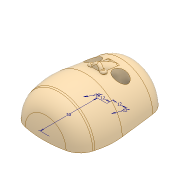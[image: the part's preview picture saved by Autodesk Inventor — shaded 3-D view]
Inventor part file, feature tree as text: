
AUTODESK INVENTOR PART (.ipt)
format: ipt  version: 2017 (Build 210142000, 142)  size: 386,560 bytes
history: native  units: mm
features: fillet x7, sketch x5, extrude x4, revolve x1, chamfer x1, thicken_offset x1
ambient origin geometry x8: Origin, YZ Plane, XZ Plane, XY Plane, X Axis, Y Axis, Z Axis, Center Point
bodies: Solid1 (feature_tree)
feature tree (19):
  revolve  "Revolution1"  [1 undecoded]
  fillet  "Fillet1"  Radius=30.0mm
  chamfer  "Chamfer1"  Distance=10.0mm Angle=45.0deg
  fillet  "Fillet2"  Radius=20.0mm
  fillet  "Fillet3"  Radius=60.0mm
  thicken_offset  "Thicken1"
  extrude  "Extrusion1"  Depth=4.0mm
  sketch  "Sketch3"  dims[d4=20.0mm d5=10.0mm d6=20.0mm d7=45.0deg d8=20.0mm d9=60.0mm]
  extrude  "Extrusion2"  Depth=1.5mm
  extrude  "Extrusion3"  Depth=1.5mm
  fillet  "Fillet4"  Radius=12.0mm
  fillet  "Fillet5"  Radius=12.0mm
  extrude  "Extrusion4"  Depth=1.5mm
  fillet  "Fillet6"  Radius=10.0mm
  fillet  "Fillet7"  Radius=10.0mm
  sketch  "Sketch1"  dims[d0=40.0mm d1=80.0mm d2=30.0mm]
  sketch  "Sketch2"  dims[d3=90.0deg]
  sketch  "Sketch4"  dims[d10=4.0mm d11=4.0mm]
  sketch  "Sketch5"  dims[d12=0.0mm d13=0.0mm d14=50.0mm d15=12.0mm d16=12.0mm d17=12.0mm d18=12.0mm d20=10.0mm d21=0.0mm d22=10.0mm d23=0.0mm d24=6.0mm d25=2.0mm d26=5.0mm d27=5.0mm d28=32.0mm d29=0.0mm d30=2.0mm d31=56.0mm d32=40.0mm d33=1.5mm]
note: 1 required parameter value undecoded (feature->parameter linkage not recoverable at this tier; creation-order binding heuristic only, values carry confidence <= 0.55)
